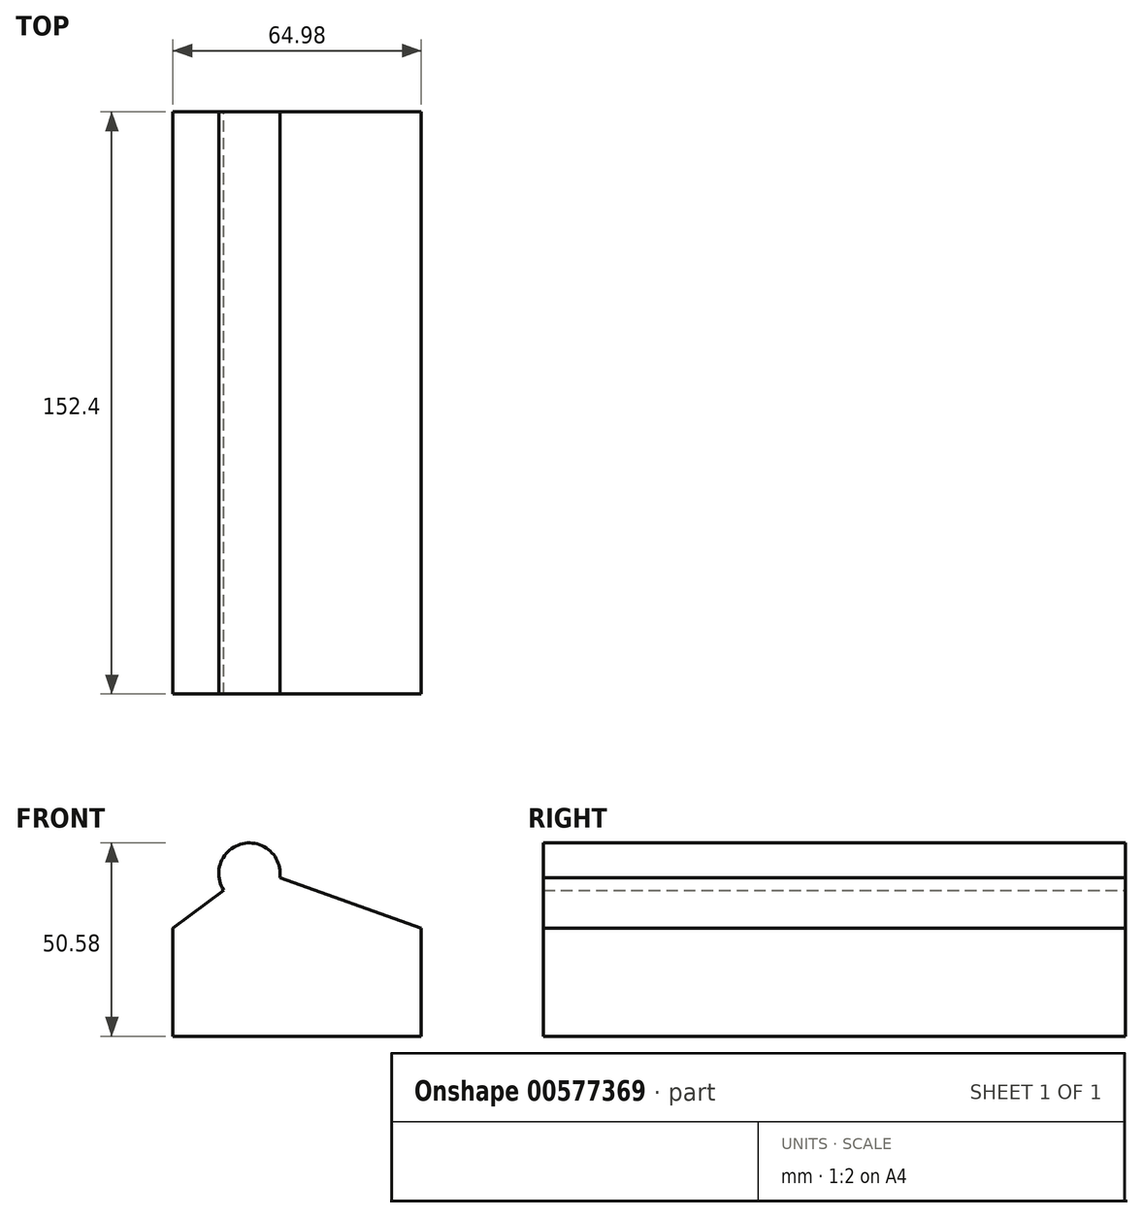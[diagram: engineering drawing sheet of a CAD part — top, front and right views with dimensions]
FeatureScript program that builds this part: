
annotation { "Feature Type Name" : "Feature", "Feature Type Description" : "" }
export const myFeature = defineFeature(function(context is Context, id is Id, definition is map)
    precondition{}
    {
        {
            var Q0;
            Q0=qCreatedBy(makeId("Front.planeOp"),FACE);
            var sketch = newSketch(context, id + "F0", { "sketchPlane" : qUnion([Q0])});
            skLineSegment(sketch, "E0.bottom", {"start": v(32.49, 14.14) * mm, "end": v(-32.49, 14.14) * mm});
            skLineSegment(sketch, "E0.top", {"start": v(32.49, -14.14) * mm, "end": v(-32.49, -14.14) * mm});
            skLineSegment(sketch, "E0.left", {"start": v(32.49, 14.14) * mm, "end": v(32.49, -14.14) * mm});
            skLineSegment(sketch, "E0.right", {"start": v(-32.49, 14.14) * mm, "end": v(-32.49, -14.14) * mm});
            skPoint(sketch, "E0.middle", {"position": v(0, 0) * mm});
            skLineSegment(sketch, "E1.bottom", {"start": v(19.25, -7.52) * mm, "end": v(-19.25, -7.52) * mm});
            skLineSegment(sketch, "E1.top", {"start": v(19.25, 7.52) * mm, "end": v(-19.25, 7.52) * mm});
            skLineSegment(sketch, "E1.left", {"start": v(19.25, -7.52) * mm, "end": v(19.25, 7.52) * mm});
            skLineSegment(sketch, "E1.right", {"start": v(-19.25, -7.52) * mm, "end": v(-19.25, 7.52) * mm});
            skLineSegment(sketch, "E2.bottom", {"start": v(0.7, 0) * mm, "end": v(0.7, 0) * mm});
            skLineSegment(sketch, "E2.top", {"start": v(0.7, 0) * mm, "end": v(0.7, 0) * mm});
            skLineSegment(sketch, "E2.left", {"start": v(0.7, 0) * mm, "end": v(0.7, 0) * mm});
            skLineSegment(sketch, "E2.right", {"start": v(0.7, 0) * mm, "end": v(0.7, 0) * mm});
            skPoint(sketch, "E2.middle", {"position": v(0.7, 0) * mm});
            skPoint(sketch, "E3", {"position": v(19.25, 0) * mm});
            skArc(sketch, "E4", {"start": v(19.25, -7.52) * mm, "mid": v(10.7, -1.95) * mm, "end": v(0.7, 0) * mm});
            skArc(sketch, "E5", {"start": v(0, 0) * mm, "mid": v(12.2, -2.81) * mm, "end": v(19.25, 7.52) * mm});
            skArc(sketch, "E6", {"start": v(0, 0) * mm, "mid": v(-10.6, -1.29) * mm, "end": v(-19.25, -7.52) * mm});
            skArc(sketch, "E7", {"start": v(-19.25, 7.52) * mm, "mid": v(-12.2, -2.81) * mm, "end": v(0, 0) * mm});
            skArc(sketch, "E8", {"start": v(19.25, 7.52) * mm, "mid": v(25.8, -3.35) * mm, "end": v(32.49, -14.14) * mm});
            skArc(sketch, "E9", {"start": v(32.49, 14.14) * mm, "mid": v(25.68, 3.42) * mm, "end": v(19.25, -7.52) * mm});
            skArc(sketch, "E10", {"start": v(-19.25, -7.52) * mm, "mid": v(-26.65, -9.27) * mm, "end": v(-32.49, -14.14) * mm});
            skArc(sketch, "E11", {"start": v(-32.49, 14.14) * mm, "mid": v(-26.65, 9.27) * mm, "end": v(-19.25, 7.52) * mm});
            skArc(sketch, "E12", {"start": v(-4.51, 27.37) * mm, "mid": v(-14.24, 36.24) * mm, "end": v(-19.25, 24.06) * mm});
            skLineSegment(sketch, "E13", {"start": v(-19.25, 24.06) * mm, "end": v(-4.51, 27.37) * mm});
            skLineSegment(sketch, "E14", {"start": v(-19.25, 24.06) * mm, "end": v(-32.49, 14.14) * mm});
            skLineSegment(sketch, "E15", {"start": v(-4.51, 27.37) * mm, "end": v(32.49, 14.14) * mm});
            skSolve(sketch);
        }
        {
            var Q0;
            Q0=makeQuery(id+"F0.imprint","IMPRINT",FACE,{"disambiguationData":[TD([[makeQuery(id+"F0.imprint","IMPRINT",EDGE,{"derivedFrom":sQuery(id+"F0.wireOp",EDGE,"E12")}),1.0]])]});
            var Q1;
            {var subQ0=sQuery(id+"F0.wireOp",EDGE,"E0.left");Q1=makeQuery(id+"F0.imprint","IMPRINT",FACE,{"disambiguationData":[TD([[makeQuery(id+"F0.imprint","IMPRINT",EDGE,{"derivedFrom":subQ0}),-1.0]])]});}
            var Q2;
            {var subQ0=sQuery(id+"F0.wireOp",EDGE,"E7");var subQ1=sQuery(id+"F0.wireOp",EDGE,"E6");var subQ3=makeQuery(id+"F0.imprint","INTERSECT",VERTEX,{"derivedFrom":[subQ1,subQ0]});Q2=makeQuery(id+"F0.imprint","IMPRINT",FACE,{"disambiguationData":[TD([[makeQuery(id+"F0.imprint","IMPRINT",EDGE,{"disambiguationData":[TD([[subQ3,1.0]])],"derivedFrom":subQ1}),1.0]])]});}
            var Q3;
            Q3=makeQuery(id+"F0.imprint","IMPRINT",FACE,{"disambiguationData":[TD([[makeQuery(id+"F0.imprint","IMPRINT",EDGE,{"derivedFrom":sQuery(id+"F0.wireOp",EDGE,"E0.bottom")}),-1.0]])]});
            var Q4;
            Q4=makeQuery(id+"F0.imprint","IMPRINT",FACE,{"disambiguationData":[TD([[makeQuery(id+"F0.imprint","IMPRINT",EDGE,{"derivedFrom":sQuery(id+"F0.wireOp",EDGE,"E0.right")}),1.0]])]});
            var Q5;
            {var subQ0=sQuery(id+"F0.wireOp",EDGE,"E1.left");Q5=makeQuery(id+"F0.imprint","IMPRINT",FACE,{"disambiguationData":[TD([[makeQuery(id+"F0.imprint","IMPRINT",EDGE,{"derivedFrom":subQ0}),1.0]])]});}
            var Q6;
            {var subQ0=sQuery(id+"F0.wireOp",EDGE,"E1.left");Q6=makeQuery(id+"F0.imprint","IMPRINT",FACE,{"disambiguationData":[TD([[makeQuery(id+"F0.imprint","IMPRINT",EDGE,{"derivedFrom":subQ0}),-1.0]])]});}
            var Q7;
            {var subQ0=sQuery(id+"F0.wireOp",EDGE,"E1.right");Q7=makeQuery(id+"F0.imprint","IMPRINT",FACE,{"disambiguationData":[TD([[makeQuery(id+"F0.imprint","IMPRINT",EDGE,{"derivedFrom":subQ0}),-1.0]])]});}
            var Q8;
            {var subQ4=sQuery(id+"F0.wireOp",EDGE,"E0.top");Q8=makeQuery(id+"F0.imprint","IMPRINT",FACE,{"disambiguationData":[TD([[makeQuery(id+"F0.imprint","IMPRINT",EDGE,{"derivedFrom":subQ4}),-1.0]])]});}
            var Q9;
            {var subQ1=sQuery(id+"F0.wireOp",EDGE,"E0.bottom");Q9=makeQuery(id+"F0.imprint","IMPRINT",FACE,{"disambiguationData":[TD([[makeQuery(id+"F0.imprint","IMPRINT",EDGE,{"derivedFrom":subQ1}),1.0]])]});}
            var Q10;
            {var subQ1=sQuery(id+"F0.wireOp",EDGE,"E1.bottom");Q10=makeQuery(id+"F0.imprint","IMPRINT",FACE,{"disambiguationData":[TD([[makeQuery(id+"F0.imprint","IMPRINT",EDGE,{"derivedFrom":subQ1}),-1.0]])]});}
            var Q11;
            {var subQ6=sQuery(id+"F0.wireOp",EDGE,"E1.top");Q11=makeQuery(id+"F0.imprint","IMPRINT",FACE,{"disambiguationData":[TD([[makeQuery(id+"F0.imprint","IMPRINT",EDGE,{"derivedFrom":subQ6}),1.0]])]});}
            extrude(context, id + "F1", {"entities" : qUnion([Q0, Q1, Q2, Q3, Q4, Q5, Q6, Q7, Q8, Q9, Q10, Q11]), "depth" : 152.4 * mm, "offsetDistance" : 25.4 * mm});
        }
    });
